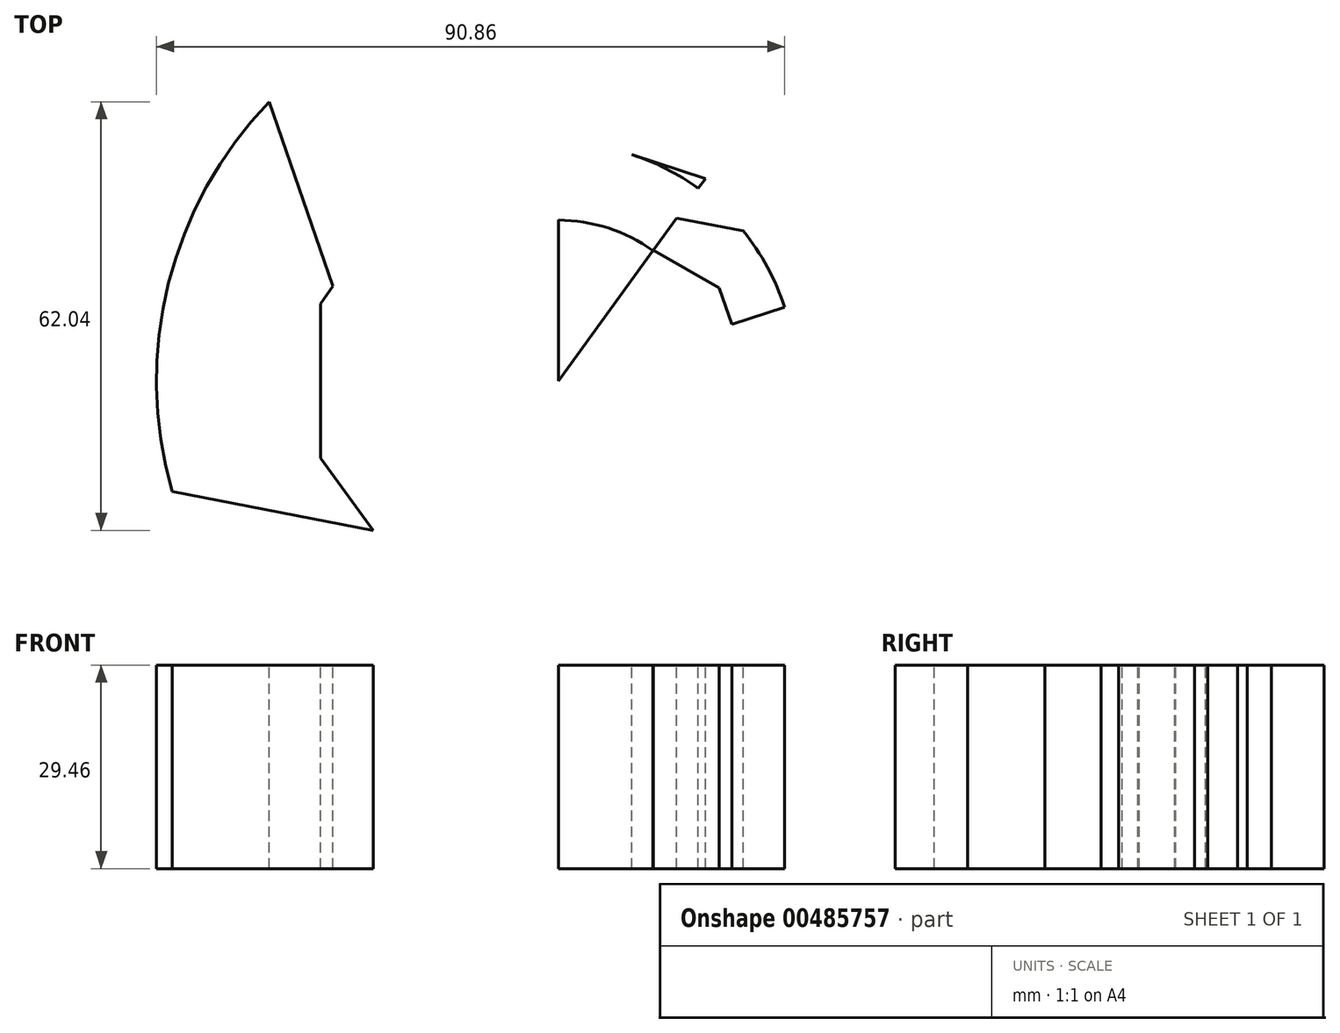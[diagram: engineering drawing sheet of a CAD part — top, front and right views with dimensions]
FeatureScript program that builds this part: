
annotation { "Feature Type Name" : "Feature", "Feature Type Description" : "" }
export const myFeature = defineFeature(function(context is Context, id is Id, definition is map)
    precondition{}
    {
        {
            var Q0;
            Q0=qCreatedBy(makeId("Top.planeOp"),FACE);
            var sketch = newSketch(context, id + "F0", { "sketchPlane" : qUnion([Q0])});
            skCircle(sketch, "E0.cCircle", {"center": v(0, 0) * mm, "radius": 23.25 * mm, "construction": true});
            skLineSegment(sketch, "E0.0", {"start": v(-23.25, -13.43) * mm, "end": v(-23.25, 13.43) * mm});
            skLineSegment(sketch, "E0.1", {"start": v(-23.25, 13.43) * mm, "end": v(0, 26.85) * mm});
            skLineSegment(sketch, "E0.2", {"start": v(0, 26.85) * mm, "end": v(23.25, 13.43) * mm});
            skLineSegment(sketch, "E0.3", {"start": v(23.25, 13.43) * mm, "end": v(23.25, -13.43) * mm});
            skLineSegment(sketch, "E0.4", {"start": v(23.25, -13.43) * mm, "end": v(0, -26.85) * mm});
            skLineSegment(sketch, "E0.5", {"start": v(0, -26.85) * mm, "end": v(-23.25, -13.43) * mm});
            skPoint(sketch, "E0.0.midPoint", {"position": v(-23.25, 0) * mm});
            skCircle(sketch, "E1.cCircle", {"center": v(0, 0) * mm, "radius": 34.42 * mm, "construction": true});
            skLineSegment(sketch, "E1.0", {"start": v(-34.42, -11.18) * mm, "end": v(-34.42, 11.18) * mm});
            skLineSegment(sketch, "E1.1", {"start": v(-34.42, 11.18) * mm, "end": v(-21.27, 29.28) * mm});
            skLineSegment(sketch, "E1.2", {"start": v(-21.27, 29.28) * mm, "end": v(0, 36.19) * mm});
            skLineSegment(sketch, "E1.3", {"start": v(0, 36.19) * mm, "end": v(21.27, 29.28) * mm});
            skLineSegment(sketch, "E1.4", {"start": v(21.27, 29.28) * mm, "end": v(34.42, 11.18) * mm});
            skLineSegment(sketch, "E1.5", {"start": v(34.42, 11.18) * mm, "end": v(34.42, -11.18) * mm});
            skLineSegment(sketch, "E1.6", {"start": v(34.42, -11.18) * mm, "end": v(21.27, -29.28) * mm});
            skLineSegment(sketch, "E1.7", {"start": v(21.27, -29.28) * mm, "end": v(0, -36.19) * mm});
            skLineSegment(sketch, "E1.8", {"start": v(0, -36.19) * mm, "end": v(-21.27, -29.28) * mm});
            skLineSegment(sketch, "E1.9", {"start": v(-21.27, -29.28) * mm, "end": v(-34.42, -11.18) * mm});
            skPoint(sketch, "E1.0.midPoint", {"position": v(-34.42, 0) * mm});
            skCircle(sketch, "E2.cCircle", {"center": v(0, 0) * mm, "radius": 58.13 * mm, "construction": true});
            skLineSegment(sketch, "E2.0", {"start": v(-58.13, -15.58) * mm, "end": v(-58.13, 15.58) * mm});
            skLineSegment(sketch, "E2.1", {"start": v(-58.13, 15.58) * mm, "end": v(-42.56, 42.56) * mm});
            skLineSegment(sketch, "E2.2", {"start": v(-42.56, 42.56) * mm, "end": v(-15.58, 58.13) * mm});
            skLineSegment(sketch, "E2.3", {"start": v(-15.58, 58.13) * mm, "end": v(15.58, 58.13) * mm});
            skLineSegment(sketch, "E2.4", {"start": v(15.58, 58.13) * mm, "end": v(42.56, 42.56) * mm});
            skLineSegment(sketch, "E2.5", {"start": v(42.56, 42.56) * mm, "end": v(58.13, 15.58) * mm});
            skLineSegment(sketch, "E2.6", {"start": v(58.13, 15.58) * mm, "end": v(58.13, -15.58) * mm});
            skLineSegment(sketch, "E2.7", {"start": v(58.13, -15.58) * mm, "end": v(42.56, -42.56) * mm});
            skLineSegment(sketch, "E2.8", {"start": v(42.56, -42.56) * mm, "end": v(15.58, -58.13) * mm});
            skLineSegment(sketch, "E2.9", {"start": v(15.58, -58.13) * mm, "end": v(-15.58, -58.13) * mm});
            skLineSegment(sketch, "E2.10", {"start": v(-15.58, -58.13) * mm, "end": v(-42.56, -42.56) * mm});
            skLineSegment(sketch, "E2.11", {"start": v(-42.56, -42.56) * mm, "end": v(-58.13, -15.58) * mm});
            skPoint(sketch, "E2.0.midPoint", {"position": v(-58.13, 0) * mm});
            skLineSegment(sketch, "E3", {"start": v(-21.27, -29.28) * mm, "end": v(21.27, 29.28) * mm});
            skLineSegment(sketch, "E4", {"start": v(-34.42, 11.18) * mm, "end": v(34.42, -11.18) * mm});
            skLineSegment(sketch, "E5", {"start": v(21.27, -29.28) * mm, "end": v(-21.27, 29.28) * mm});
            skLineSegment(sketch, "E6", {"start": v(0, -36.19) * mm, "end": v(0, 36.19) * mm});
            skLineSegment(sketch, "E7", {"start": v(-34.42, -11.18) * mm, "end": v(34.42, 11.18) * mm});
            skLineSegment(sketch, "E8", {"start": v(-23.25, -13.43) * mm, "end": v(-42.56, 42.56) * mm});
            skLineSegment(sketch, "E9", {"start": v(-23.25, 13.43) * mm, "end": v(15.58, 58.13) * mm});
            skLineSegment(sketch, "E10", {"start": v(0, 26.85) * mm, "end": v(58.13, 15.58) * mm});
            skLineSegment(sketch, "E11", {"start": v(23.25, 13.43) * mm, "end": v(42.56, -42.56) * mm});
            skLineSegment(sketch, "E12", {"start": v(23.25, -13.43) * mm, "end": v(-15.58, -58.13) * mm});
            skLineSegment(sketch, "E13", {"start": v(0, -26.85) * mm, "end": v(-58.13, -15.58) * mm});
            skCircle(sketch, "E14", {"center": v(0, 0) * mm, "radius": 23.25 * mm});
            skCircle(sketch, "E15", {"center": v(0, 0) * mm, "radius": 34.42 * mm});
            skCircle(sketch, "E16", {"center": v(0, 0) * mm, "radius": 58.13 * mm});
            skSolve(sketch);
        }
        {
            var Q0;
            {var subQ0=sQuery(id+"F0.wireOp",EDGE,"E13");var subQ1=sQuery(id+"F0.wireOp",EDGE,"E1.9");var subQ2=makeQuery(id+"F0.imprint","INTERSECT",VERTEX,{"derivedFrom":[subQ1,subQ0]});Q0=makeQuery(id+"F0.imprint","IMPRINT",FACE,{"disambiguationData":[TD([[makeQuery(id+"F0.imprint","IMPRINT",EDGE,{"disambiguationData":[TD([[subQ2,-1.0]])],"derivedFrom":subQ1}),1.0]])]});}
            var Q1;
            {var subQ0=sQuery(id+"F0.wireOp",EDGE,"E14");var subQ6=makeQuery(id+"F0.imprint","INTERSECT",VERTEX,{"derivedFrom":[sQuery(id+"F0.wireOp",EDGE,"E0.2"),subQ0]});Q1=makeQuery(id+"F0.imprint","IMPRINT",FACE,{"disambiguationData":[TD([[makeQuery(id+"F0.imprint","IMPRINT",EDGE,{"disambiguationData":[TD([[subQ6,1.0]])],"derivedFrom":subQ0}),1.0]])]});}
            var Q2;
            {var subQ1=sQuery(id+"F0.wireOp",EDGE,"E3");var subQ6=sQuery(id+"F0.wireOp",EDGE,"E0.2");var subQ8=makeQuery(id+"F0.imprint","INTERSECT",VERTEX,{"derivedFrom":[subQ6,subQ1]});Q2=makeQuery(id+"F0.imprint","IMPRINT",FACE,{"disambiguationData":[TD([[makeQuery(id+"F0.imprint","IMPRINT",EDGE,{"disambiguationData":[TD([[subQ8,-1.0]])],"derivedFrom":subQ1}),-1.0]])]});}
            var Q3;
            {var subQ1=sQuery(id+"F0.wireOp",EDGE,"E1.3");var subQ3=sQuery(id+"F0.wireOp",EDGE,"E15");var subQ4=makeQuery(id+"F0.imprint","INTERSECT",VERTEX,{"derivedFrom":[subQ1,subQ3]});Q3=makeQuery(id+"F0.imprint","IMPRINT",FACE,{"disambiguationData":[TD([[makeQuery(id+"F0.imprint","IMPRINT",EDGE,{"disambiguationData":[TD([[subQ4,1.0]])],"derivedFrom":subQ3}),-1.0]])]});}
            extrude(context, id + "F1", {"entities" : qUnion([Q0, Q1, Q2, Q3]), "oppositeDirection" : true, "depth" : 29.46 * mm, "offsetDistance" : 25.4 * mm});
        }
    });
